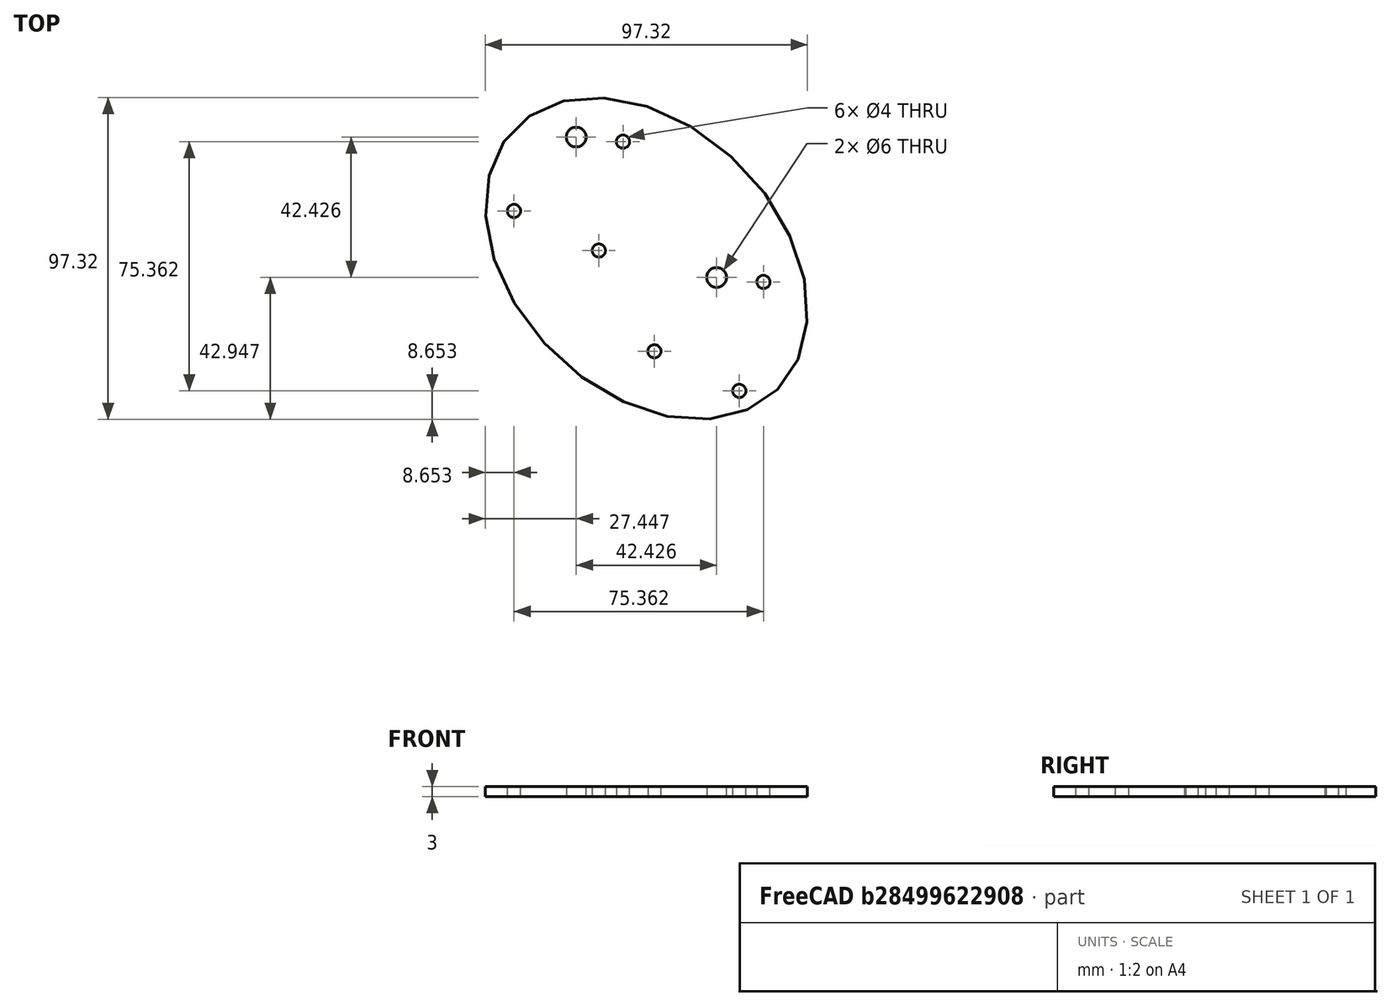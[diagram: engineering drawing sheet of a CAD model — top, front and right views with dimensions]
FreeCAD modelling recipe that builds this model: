
FCSTD DOCUMENT  (FreeCAD 0.19R24276 (Git))
Label: plate_for_kran_holder
License: All rights reserved
LicenseURL: http://en.wikipedia.org/wiki/All_rights_reserved
objects: Sketcher::SketchObject×1, PartDesign::Pad×1, PartDesign::Body×1
note: 4 computed .brp shape members not serialized (recipe doc carries the construction recipe); baked Part::Feature solids carry a one-line shape summary decoded from their .brp

FEATURE [Sketcher::SketchObject] Sketch
  FullyConstrained = false
  MapMode = 5
  Support = -> [XY_Plane]
  sketch-geometry (28):
    g0: LineSegment StartX=-21.2132 StartY=21.2132 StartZ=0 EndX=0 EndY=0 EndZ=0
    g1: Circle CenterX=-21.2132 CenterY=21.2132 CenterZ=0 NormalX=0 NormalY=0 NormalZ=1 AngleXU=0 Radius=26
    g2: LineSegment StartX=0 StartY=0 StartZ=0 EndX=21.2132 EndY=-21.2132 EndZ=0
    g3: Circle CenterX=21.2132 CenterY=-21.2132 CenterZ=0 NormalX=0 NormalY=0 NormalZ=1 AngleXU=0 Radius=26
    g4: LineSegment StartX=-21.2132 StartY=21.2132 StartZ=0 EndX=-7.07107 EndY=35.3553 EndZ=0
    g5: LineSegment StartX=-21.2132 StartY=21.2132 StartZ=0 EndX=13.757 EndY=21.2132 EndZ=0
    g6: Circle CenterX=-7.07107 CenterY=35.3553 CenterZ=0 NormalX=0 NormalY=0 NormalZ=1 AngleXU=0 Radius=2
    g7: LineSegment StartX=-21.2132 StartY=21.2132 StartZ=0 EndX=-40.0071 EndY=14.3728 EndZ=0
    g8: LineSegment StartX=-21.2132 StartY=21.2132 StartZ=0 EndX=-14.3728 EndY=2.41935 EndZ=0
    g9: Circle CenterX=-40.0071 CenterY=14.3728 CenterZ=0 NormalX=0 NormalY=0 NormalZ=1 AngleXU=0 Radius=2
    g10: Circle CenterX=-14.3728 CenterY=2.41935 CenterZ=0 NormalX=0 NormalY=0 NormalZ=1 AngleXU=0 Radius=0
    g11: Circle CenterX=-14.3728 CenterY=2.41935 CenterZ=0 NormalX=0 NormalY=0 NormalZ=1 AngleXU=0 Radius=2
    g12: LineSegment StartX=21.2132 StartY=-21.2132 StartZ=0 EndX=35.3553 EndY=-7.07107 EndZ=0
    g13: LineSegment StartX=21.2132 StartY=-21.2132 StartZ=0 EndX=28.0536 EndY=-40.0071 EndZ=0
    g14: LineSegment StartX=21.2132 StartY=-21.2132 StartZ=0 EndX=2.41935 EndY=-28.0536 EndZ=0
    g15: LineSegment StartX=21.2132 StartY=-21.2132 StartZ=0 EndX=77.3277 EndY=-21.2132 EndZ=0
    g16: Circle CenterX=35.3553 CenterY=-7.07107 CenterZ=0 NormalX=0 NormalY=0 NormalZ=1 AngleXU=0 Radius=2
    g17: Circle CenterX=2.41935 CenterY=-28.0536 CenterZ=0 NormalX=0 NormalY=0 NormalZ=1 AngleXU=0 Radius=2
    g18: Circle CenterX=28.0536 CenterY=-40.0071 CenterZ=0 NormalX=0 NormalY=0 NormalZ=1 AngleXU=0 Radius=2
    g19: Ellipse CenterX=0 CenterY=0 CenterZ=0 NormalX=0 NormalY=0 NormalZ=1 MajorRadius=56 MinorRadius=40 AngleXU=-0.785398
    g20: LineSegment StartX=39.598 StartY=-39.598 StartZ=0 EndX=-39.598 EndY=39.598 EndZ=0
    g21: LineSegment StartX=28.2843 StartY=28.2843 StartZ=0 EndX=-28.2843 EndY=-28.2843 EndZ=0
    g22: GeomPoint X=27.7128 Y=-27.7128 Z=0
    g23: GeomPoint X=-27.7128 Y=27.7128 Z=0
    g24: LineSegment StartX=-21.2132 StartY=21.2132 StartZ=0 EndX=-21.2132 EndY=36.7132 EndZ=0
    g25: Circle CenterX=-21.2132 CenterY=36.7132 CenterZ=0 NormalX=0 NormalY=0 NormalZ=1 AngleXU=0 Radius=3
    g26: LineSegment StartX=21.2132 StartY=-21.2132 StartZ=0 EndX=21.2132 EndY=-5.7132 EndZ=0
    g27: Circle CenterX=21.2132 CenterY=-5.7132 CenterZ=0 NormalX=0 NormalY=0 NormalZ=1 AngleXU=0 Radius=3
  constraints (61):
    c: Angle(g-2,g0) = 0.785398
    c: Diameter(g1) = 52
    c: Coincident(g1,g0)
    c: Distance(g0) = 30
    c: Angle(g2,g-1) = 0.785398
    c: Coincident(g3,g2)
    c: Diameter(g3) = 52
    c: Distance(g2) = 30
    c: Coincident(g4,g0)
    c: Coincident(g5,g0)
    c: Horizontal(g5)
    c: Angle(g5,g4) = 0.785398
    c: Distance(g4) = 20
    c: Coincident(g6,g4)
    c: Diameter(g6) = 4
    c: Coincident(g7,g0)
    c: Coincident(g8,g0)
    c: Equal(g7,g4)
    c: Equal(g8,g7)
    c: Coincident(g9,g7)
    c: Coincident(g10,g8)
    c: Tangent(g10,g8)
    c: Coincident(g11,g8)
    c: Equal(g9,g11)
    c: Equal(g11,g6)
    c: Angle(g8,g5) = 1.22173
    c: Angle(g7,g5) = 2.79253
    c: Coincident(g12,g2)
    c: Coincident(g13,g2)
    c: Coincident(g14,g2)
    c: Equal(g14,g12)
    c: Equal(g12,g13)
    c: Equal(g13,g8)
    c: Coincident(g15,g2)
    c: Horizontal(g15)
    c: Angle(g15,g12) = 0.785398
    c: Angle(g13,g15) = 1.22173
    c: Angle(g14,g15) = 2.79253
    c: Coincident(g16,g12)
    c: Coincident(g17,g14)
    c: Coincident(g18,g13)
    c: Equal(g6,g16)
    c: Equal(g16,g17)
    c: Equal(g17,g18)
    c: InternalAlignment(g20-g23 -> g19) x4
    c: Angle(g-1,g21) = 0.785398
    c: Distance(g20) = 112
    c: Distance(g21) = 80
    c: Coincident(g24,g0)
    c: Vertical(g24)
    c: Coincident(g25,g24)
    c: Diameter(g25) = 6
    c: Coincident(g26,g2)
    c: Vertical(g26)
    c: Coincident(g27,g26)
    c: Diameter(g27) = 6
    c: DistanceY(g26,g26) = 15.5
    c: DistanceY(g24,g24) = 15.5
    c: Coincident(g2,g19)
    c: Coincident(g0,g19)
    c: Coincident(g-1,g19)
FEATURE [PartDesign::Pad] Pad
  Direction = (1,1,1)
  Length = 3
  Length2 = 100
  Profile = -> Sketch
  Type = 0
FEATURE [PartDesign::Body] Body
  Group = -> [Sketch,Pad]
  Origin = -> Origin
  Tip = -> Pad
